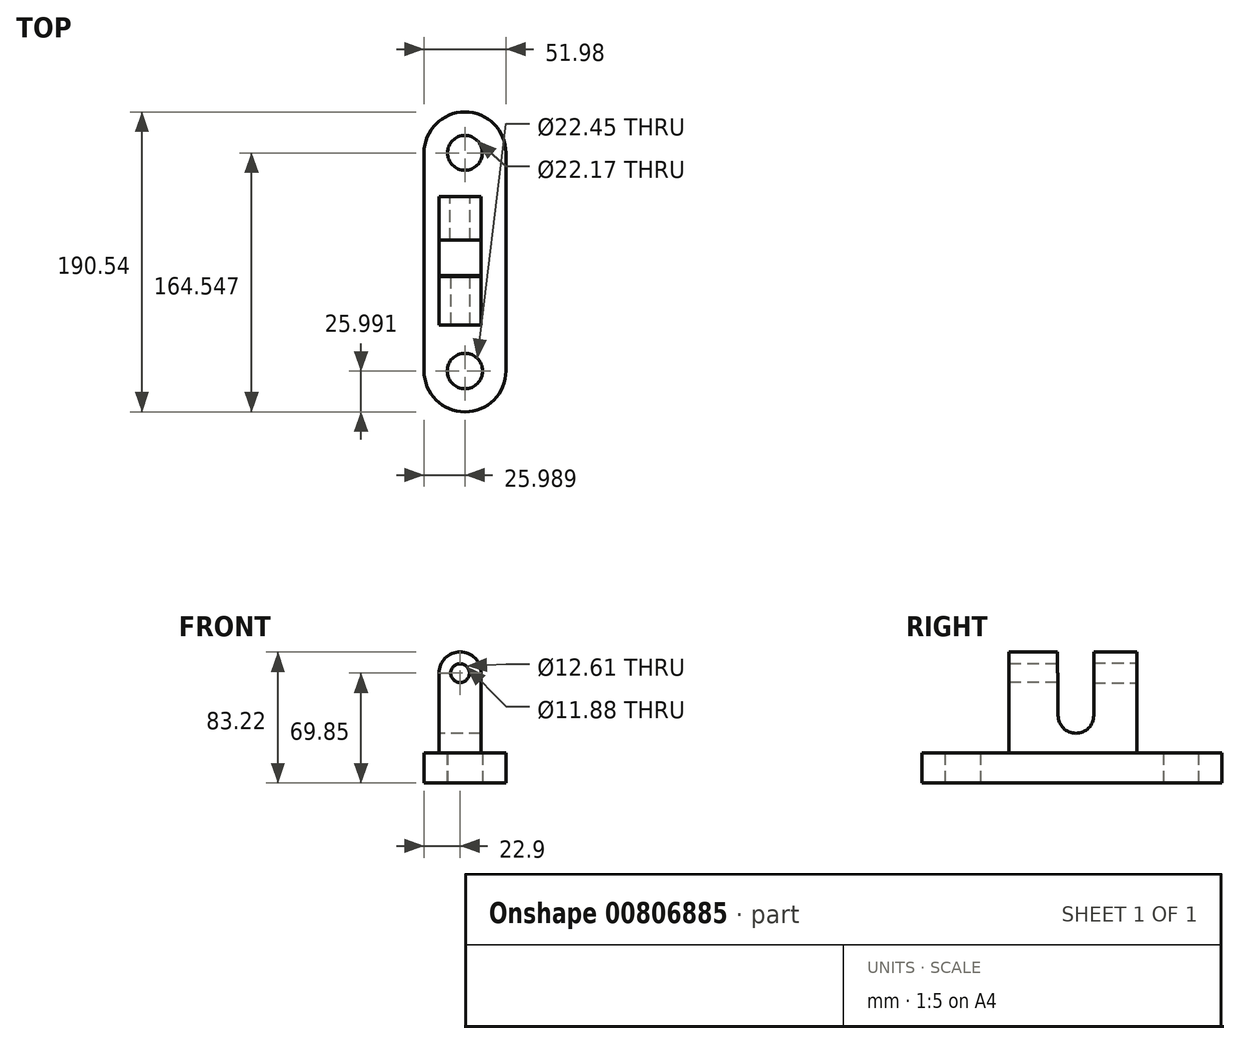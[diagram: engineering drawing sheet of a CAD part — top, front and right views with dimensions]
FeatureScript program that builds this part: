
annotation { "Feature Type Name" : "Feature", "Feature Type Description" : "" }
export const myFeature = defineFeature(function(context is Context, id is Id, definition is map)
    precondition{}
    {
        {
            var Q0;
            Q0=qCreatedBy(makeId("Top.planeOp"),FACE);
            var sketch = newSketch(context, id + "F0", { "sketchPlane" : qUnion([Q0])});
            skLineSegment(sketch, "E0.left", {"start": v(-18.1, -71.3) * mm, "end": v(-18.1, 67.26) * mm});
            skLineSegment(sketch, "E0.right", {"start": v(33.87, -71.3) * mm, "end": v(33.87, 67.26) * mm});
            skArc(sketch, "E1", {"start": v(33.87, 67.26) * mm, "mid": v(7.88, 93.25) * mm, "end": v(-18.1, 67.26) * mm});
            skArc(sketch, "E2", {"start": v(-18.1, -71.3) * mm, "mid": v(7.88, -97.29) * mm, "end": v(33.87, -71.3) * mm});
            skCircle(sketch, "E3", {"center": v(7.88, -71.3) * mm, "radius": 11.23 * mm});
            skCircle(sketch, "E4", {"center": v(7.88, 67.26) * mm, "radius": 11.09 * mm});
            skSolve(sketch);
        }
        {
            var Q0;
            Q0=makeQuery(id+"F0.imprint","IMPRINT",FACE,{"disambiguationData":[TD([[makeQuery(id+"F0.imprint","IMPRINT",EDGE,{"derivedFrom":sQuery(id+"F0.wireOp",EDGE,"E0.left")}),-1.0]])]});
            extrude(context, id + "F1", {"entities" : qUnion([Q0]), "depth" : 19.05 * mm, "offsetDistance" : 25.4 * mm});
        }
        {
            var Q0;
            Q0=makeQuery(id+"F1.opExtrude","CAP_FACE",FACE,{"disambiguationData":[OSD([sQuery(id+"F0.wireOp",EDGE,"E0.left"),sQuery(id+"F0.wireOp",EDGE,"E0.right"),sQuery(id+"F0.wireOp",EDGE,"E1"),sQuery(id+"F0.wireOp",EDGE,"E2"),sQuery(id+"F0.wireOp",EDGE,"E3"),sQuery(id+"F0.wireOp",EDGE,"E4")])],"isStart":false});
            var sketch = newSketch(context, id + "F2", { "sketchPlane" : qUnion([Q0])});
            skLineSegment(sketch, "E5.bottom", {"start": v(-8.58, -42.03) * mm, "end": v(18.16, -42.03) * mm});
            skLineSegment(sketch, "E5.top", {"start": v(-8.58, 39.38) * mm, "end": v(18.16, 39.38) * mm});
            skLineSegment(sketch, "E5.left", {"start": v(-8.58, -42.03) * mm, "end": v(-8.58, 39.38) * mm});
            skLineSegment(sketch, "E5.right", {"start": v(18.16, -42.03) * mm, "end": v(18.16, 39.38) * mm});
            skSolve(sketch);
        }
        {
            var Q0;
            Q0=makeQuery(id+"F2.imprint","IMPRINT",FACE,{"disambiguationData":[TD([[makeQuery(id+"F2.imprint","IMPRINT",EDGE,{"derivedFrom":sQuery(id+"F2.wireOp",EDGE,"E5.bottom")}),1.0]])]});
            extrude(context, id + "F3", {"entities" : qUnion([Q0]), "operationType" : NewBodyOperationType.ADD, "depth" : 50.8 * mm, "offsetDistance" : 25.4 * mm});
        }
        {
            var Q0;
            Q0=makeQuery(id+"F3.opExtrude","SWEPT_FACE",FACE,{"disambiguationData":[OSD([sQuery(id+"F2.wireOp",EDGE,"E5.left")])]});
            var sketch = newSketch(context, id + "F4", { "sketchPlane" : qUnion([Q0])});
            skLineSegment(sketch, "E6.bottom", {"start": v(-11.9, 69.85) * mm, "end": v(10.69, 69.85) * mm});
            skLineSegment(sketch, "E6.left", {"start": v(-11.9, 69.85) * mm, "end": v(-11.9, 42.9) * mm});
            skLineSegment(sketch, "E6.right", {"start": v(10.69, 69.85) * mm, "end": v(10.69, 42.9) * mm});
            skArc(sketch, "E7", {"start": v(-11.9, 42.9) * mm, "mid": v(-0.6, 31.6) * mm, "end": v(10.69, 42.9) * mm});
            skSolve(sketch);
        }
        {
            var Q0;
            Q0=makeQuery(id+"F4.imprint","IMPRINT",FACE,{"disambiguationData":[TD([[makeQuery(id+"F4.imprint","IMPRINT",EDGE,{"derivedFrom":sQuery(id+"F4.wireOp",EDGE,"E6.bottom")}),1.0]])]});
            extrude(context, id + "F5", {"entities" : qUnion([Q0]), "operationType" : NewBodyOperationType.REMOVE, "endBound" : BoundingType.THROUGH_ALL, "oppositeDirection" : true, "depth" : 25.4 * mm, "offsetDistance" : 25.4 * mm});
        }
        {
            var Q0;
            Q0=makeQuery(id+"F3.opExtrude","SWEPT_FACE",FACE,{"disambiguationData":[OSD([sQuery(id+"F2.wireOp",EDGE,"E5.top")])]});
            var sketch = newSketch(context, id + "F6", { "sketchPlane" : qUnion([Q0])});
            skArc(sketch, "E8", {"start": v(8.58, 69.85) * mm, "mid": v(-4.79, 83.22) * mm, "end": v(-18.16, 69.85) * mm});
            skCircle(sketch, "E9", {"center": v(-4.79, 69.85) * mm, "radius": 6.3 * mm});
            skSolve(sketch);
        }
        {
            var Q0;
            Q0 = qSketchRegion(id + "F6", true);
            var Q1;
            Q1=makeQuery(id+"F6.imprint","IMPRINT",FACE,{"disambiguationData":[TD([[makeQuery(id+"F6.imprint","IMPRINT",EDGE,{"derivedFrom":sQuery(id+"F6.wireOp",EDGE,"E8")}),1.0]])]});
            extrude(context, id + "F7", {"entities" : qUnion([Q0, Q1]), "operationType" : NewBodyOperationType.ADD, "oppositeDirection" : true, "depth" : 27.43 * mm, "offsetDistance" : 25.4 * mm});
        }
        {
            var Q0;
            {var subQ0=sQuery(id+"F6.wireOp",EDGE,"E9");var subQ1=makeQuery(id+"F3.opExtrude","CAP_EDGE",EDGE,{"disambiguationData":[OSD([sQuery(id+"F2.wireOp",EDGE,"E5.top")])],"isStart":false});var subQ2=makeQuery(id+"F6.imprint","INTERSECT",VERTEX,{"disambiguationData":[OD(0.0)],"derivedFrom":[subQ1,subQ0]});Q0=makeQuery(id+"F6.imprint","IMPRINT",FACE,{"disambiguationData":[TD([[makeQuery(id+"F6.imprint","IMPRINT",EDGE,{"disambiguationData":[TD([[subQ2,1.0]])],"derivedFrom":subQ0}),1.0]])]});}
            var Q1;
            {var subQ0=sQuery(id+"F6.wireOp",EDGE,"E9");var subQ1=makeQuery(id+"F3.opExtrude","CAP_EDGE",EDGE,{"disambiguationData":[OSD([sQuery(id+"F2.wireOp",EDGE,"E5.top")])],"isStart":false});var subQ2=makeQuery(id+"F6.imprint","INTERSECT",VERTEX,{"disambiguationData":[OD(0.0)],"derivedFrom":[subQ1,subQ0]});Q1=makeQuery(id+"F6.imprint","IMPRINT",FACE,{"disambiguationData":[TD([[makeQuery(id+"F6.imprint","IMPRINT",EDGE,{"disambiguationData":[TD([[subQ2,-1.0]])],"derivedFrom":subQ0}),1.0]])]});}
            extrude(context, id + "F8", {"entities" : qUnion([Q0, Q1]), "operationType" : NewBodyOperationType.REMOVE, "endBound" : BoundingType.THROUGH_ALL, "oppositeDirection" : true, "depth" : 25.4 * mm, "offsetDistance" : 25.4 * mm});
        }
        {
            var Q0;
            Q0=makeQuery(id+"F3.opExtrude","SWEPT_FACE",FACE,{"disambiguationData":[OSD([sQuery(id+"F2.wireOp",EDGE,"E5.bottom")])]});
            var sketch = newSketch(context, id + "F9", { "sketchPlane" : qUnion([Q0])});
            skArc(sketch, "E10", {"start": v(18.16, 69.85) * mm, "mid": v(4.79, 83.22) * mm, "end": v(-8.58, 69.85) * mm});
            skCircle(sketch, "E11", {"center": v(4.79, 69.85) * mm, "radius": 5.94 * mm});
            skSolve(sketch);
        }
        {
            var Q0;
            Q0=makeQuery(id+"F9.imprint","IMPRINT",FACE,{"disambiguationData":[TD([[makeQuery(id+"F9.imprint","IMPRINT",EDGE,{"derivedFrom":sQuery(id+"F9.wireOp",EDGE,"E10")}),1.0]])]});
            extrude(context, id + "F10", {"entities" : qUnion([Q0]), "operationType" : NewBodyOperationType.ADD, "oppositeDirection" : true, "depth" : 30.73 * mm, "offsetDistance" : 25.4 * mm});
        }
    });
